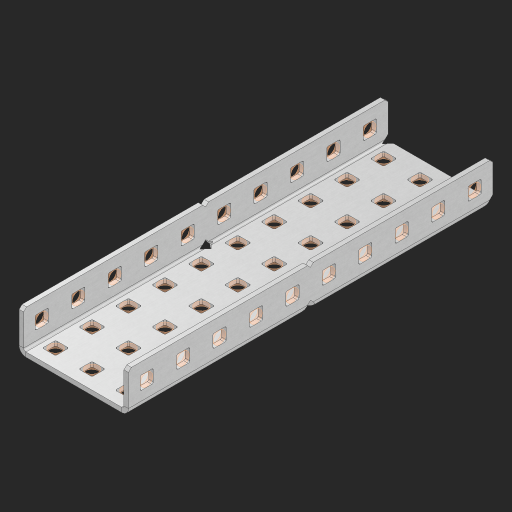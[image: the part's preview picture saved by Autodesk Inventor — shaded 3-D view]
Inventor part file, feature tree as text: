
AUTODESK INVENTOR PART (.ipt)
format: ipt  version: 2023 (Build 270158000, 158)  size: 919,552 bytes
history: native  units: in
note: dims shown in document units (in); Inventor stores cm internally (conversion verified against a paired STEP export)
features: other x55, extrude x49, sheet_metal_op x10, sketch x8, mirror x1, pattern_linear x1, chamfer x1
ambient origin geometry x8: Origin, YZ Plane, XZ Plane, XY Plane, X Axis, Y Axis, Z Axis, Center Point
bodies: Solid1 (feature_tree), Body (feature_tree)
feature tree (125):
  other  "Flange Pattern Plane"
  sheet_metal_op  "Flange Pattern"
  sheet_metal_op  "Body Pattern"
  other  "Arc Length"
  mirror  "Notch Mirror"
  pattern_linear  "Notch Pattern"  Spacing1=0.25in  [1 undecoded]
  chamfer  "End Chamfer"
  extrude  "Half Cut"  Depth=0.0625in
  sketch  "Sketch1"  dims[d0=1.5in]
  other  "Plate1"
  sketch  "Sketch2"  dims[d1=5.0in]
  other  "Plate2"
  sheet_metal_op  "Bend1"
  sheet_metal_op  "Corner1"
  sketch  "Sketch3"  dims[d2=0.0625in]
  other  "Flange Pattern Sketch"
  sketch  "Sketch7"  dims[d3=0.0625in]
  other  "Srf1"
  other  "Srf2"
  sketch  "Sketch8"  dims[d4=0.0312in]
  sketch  "Sketch9"  dims[d5=0.125in]
  other  "Srf91"
  sheet_metal_op  "Body Pattern Sketch"
  other  "Srf92"
  sketch  "Sketch13"  dims[d6=0.0625in]
  sketch  "Sketch14"  dims[d7=0.5in d8=90.0deg d9=0.0312in d10=0.25in d11=0.0625in d12=0.0625in d16=0.182in d17=0.02in d18=0.0625in d19=0.0in d20=0.25in d21=0.25in d46=0.172in d47=1.0in d48=0.0in d49=0.182in d50=0.02in d51=0.25in d52=0.25in d53=0.0625in d54=0.0in d55=0.172in d56=1.0in d57=0.0in d60=3.937in d62=0.5in d63=1.1811in d65=0.5in d85=0.1473in d86=0.1782in d88=0.04in d89=0.0625in d90=0.0in d91=0.04in d92=0.0491in d95=2.5in d96=0.04in d97=0.25in d98=45.0deg d101=0.0in d102=2.497in d131=1.5in d132=3.937in d134=0.5in d139=0.5in]
  other  "Srf856"
  other  "Srf1310"
  other  "Srf1311"
  other  "Srf1312"
  other  "Srf1376"
  other  "Srf1377"
  other  "Srf1728"
  other  "Srf1755"
  other  "Srf1878"
  other  "Srf1879"
  other  "Srf1880"
  other  "Srf1881"
  other  "Srf1882"
  other  "Srf1883"
  other  "Srf1884"
  other  "Srf1885"
  other  "Srf1886"
  other  "Srf1887"
  other  "Srf1888"
  other  "Srf1889"
  other  "Srf1890"
  other  "Srf1891"
  other  "Srf1942"
  other  "Srf1943"
  other  "Srf1944"
  other  "Srf1945"
  other  "Srf1946"
  other  "Srf1947"
  other  "Srf1948"
  other  "Srf1949"
  other  "Srf1950"
  other  "Srf1951"
  other  "Srf1952"
  other  "Srf1953"
  other  "Srf1954"
  other  "Srf1955"
  other  "Srf1956"
  other  "Srf1957"
  other  "Srf1958"
  other  "Srf1959"
  other  "Srf1960"
  other  "Srf1961"
  other  "Srf1962"
  other  "Srf1963"
  other  "Srf1964"
  other  "Srf1965"
  sheet_metal_op  "Flange Stamp"
  sheet_metal_op  "Flange Circle"
  sheet_metal_op  "Body Stamp"
  sheet_metal_op  "Body Circle"
  sheet_metal_op  "Notch"
  extrude  "ExtrusionSrf2"  Depth=0.0625in
  extrude  "ExtrusionSrf92"  Depth=1.5in
  extrude  "ExtrusionSrf856"  Depth=0.02in
  extrude  "ExtrusionSrf1310"  Depth=0.0625in
  extrude  "ExtrusionSrf1311"  TaperAngle=0.0deg  [1 undecoded]
  extrude  "ExtrusionSrf1312"  Depth=0.25in
  extrude  "ExtrusionSrf1376"  Depth=0.25in
  extrude  "ExtrusionSrf1377"  Depth=1.5in
  extrude  "ExtrusionSrf1728"  Depth=1.5in TaperAngle=0.0deg
  extrude  "ExtrusionSrf1755"  Depth=1.5in
  extrude  "ExtrusionSrf1878"  Depth=0.02in
  extrude  "ExtrusionSrf1879"  Depth=0.25in
  extrude  "ExtrusionSrf1880"  Depth=0.25in
  extrude  "ExtrusionSrf1881"  Depth=0.0625in
  extrude  "ExtrusionSrf1882"  TaperAngle=0.0deg  [1 undecoded]
  extrude  "ExtrusionSrf1883"  Depth=1.5in
  extrude  "ExtrusionSrf1884"  Depth=1.5in TaperAngle=0.0deg
  extrude  "ExtrusionSrf1885"  Depth=1.5in
  extrude  "ExtrusionSrf1886"  Depth=1.5in
  extrude  "ExtrusionSrf1887"  Depth=1.5in
  extrude  "ExtrusionSrf1888"  Depth=1.5in
  extrude  "ExtrusionSrf1889"  Depth=1.5in
  extrude  "ExtrusionSrf1890"  Depth=0.0625in
  extrude  "ExtrusionSrf1891"  TaperAngle=0.0deg  [1 undecoded]
  extrude  "ExtrusionSrf1942"  Depth=1.5in
  extrude  "ExtrusionSrf1943"  Depth=1.5in
  extrude  "ExtrusionSrf1944"  Depth=1.5in
  extrude  "ExtrusionSrf1945"  Depth=0.25in TaperAngle=45.0deg
  extrude  "ExtrusionSrf1946"  TaperAngle=0.0deg  [1 undecoded]
  extrude  "ExtrusionSrf1947"  Depth=1.5in
  extrude  "ExtrusionSrf1948"  Depth=1.5in
  extrude  "ExtrusionSrf1949"  Depth=1.5in
  extrude  "ExtrusionSrf1950"  Depth=1.5in
  extrude  "ExtrusionSrf1951"  Depth=1.5in
  extrude  "ExtrusionSrf1952"  [1 undecoded]
  extrude  "ExtrusionSrf1953"  [1 undecoded]
  extrude  "ExtrusionSrf1954"  [1 undecoded]
  extrude  "ExtrusionSrf1955"  [1 undecoded]
  extrude  "ExtrusionSrf1956"  [1 undecoded]
  extrude  "ExtrusionSrf1957"  [1 undecoded]
  extrude  "ExtrusionSrf1958"  [1 undecoded]
  extrude  "ExtrusionSrf1959"  [1 undecoded]
  extrude  "ExtrusionSrf1960"  [1 undecoded]
  extrude  "ExtrusionSrf1961"  [1 undecoded]
  extrude  "ExtrusionSrf1962"  [1 undecoded]
  extrude  "ExtrusionSrf1963"  [1 undecoded]
  extrude  "ExtrusionSrf1964"  [1 undecoded]
  extrude  "ExtrusionSrf1965"  [1 undecoded]
note: 19 required parameter values undecoded (feature->parameter linkage not recoverable at this tier; creation-order binding heuristic only, values carry confidence <= 0.55)
